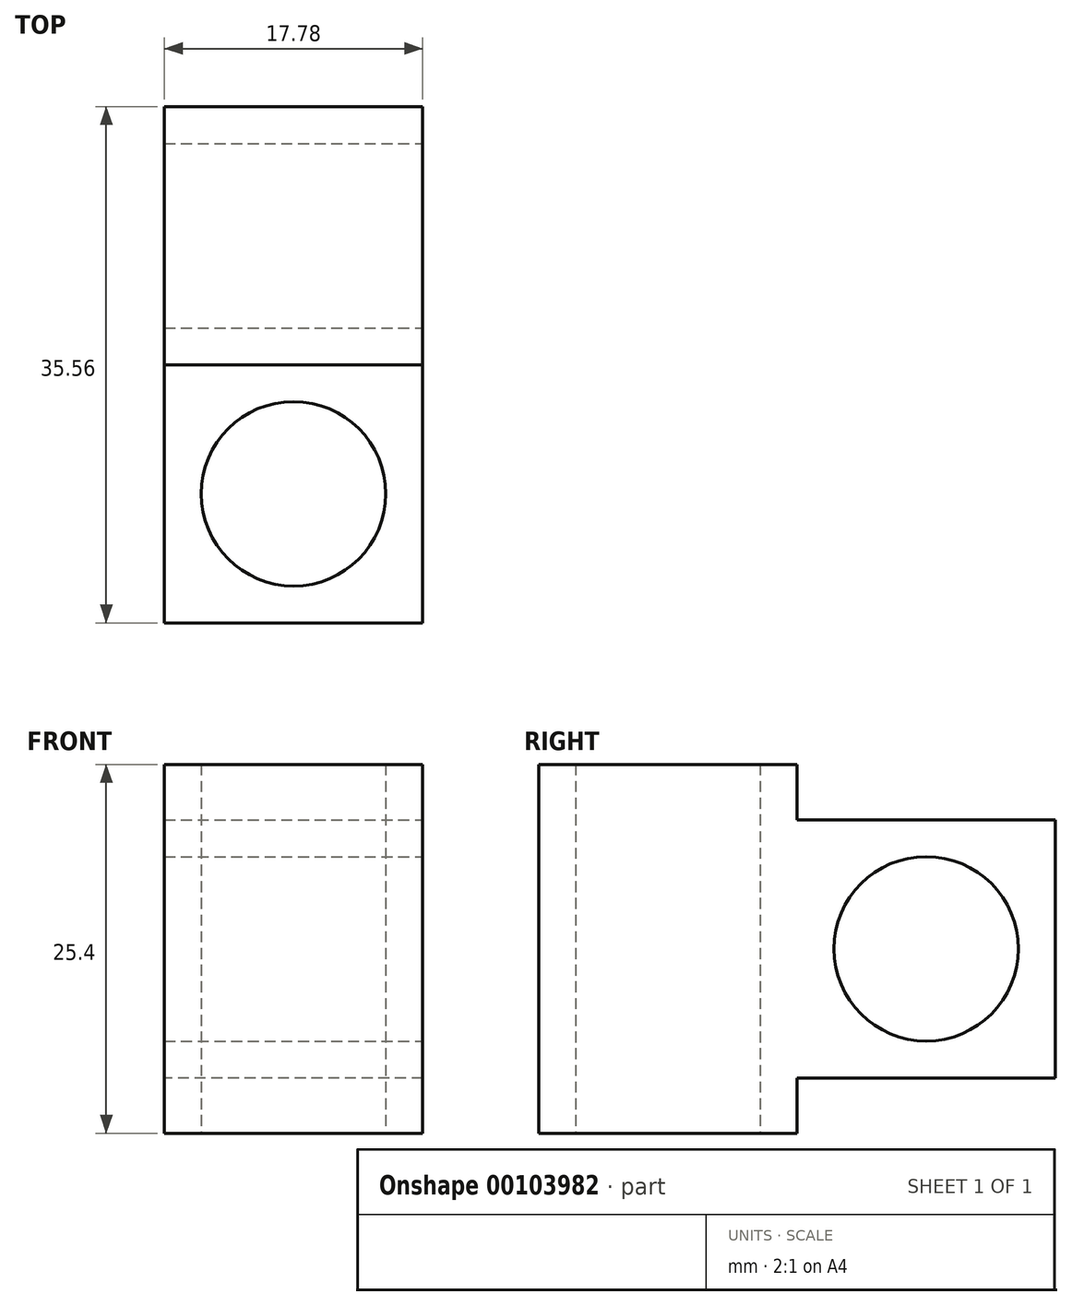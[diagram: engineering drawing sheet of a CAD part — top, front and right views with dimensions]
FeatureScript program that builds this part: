
annotation { "Feature Type Name" : "Feature", "Feature Type Description" : "" }
export const myFeature = defineFeature(function(context is Context, id is Id, definition is map)
    precondition{}
    {
        {
            var Q0;
            Q0=qCreatedBy(makeId("Top.planeOp"),FACE);
            var sketch = newSketch(context, id + "F0", { "sketchPlane" : qUnion([Q0])});
            skCircle(sketch, "E0", {"center": v(-39.15, -30.11) * mm, "radius": 6.35 * mm});
            skLineSegment(sketch, "E1.bottom", {"start": v(-30.26, -21.22) * mm, "end": v(-48.04, -21.22) * mm});
            skLineSegment(sketch, "E1.top", {"start": v(-30.26, -39) * mm, "end": v(-48.04, -39) * mm});
            skLineSegment(sketch, "E1.left", {"start": v(-30.26, -21.22) * mm, "end": v(-30.26, -39) * mm});
            skLineSegment(sketch, "E1.right", {"start": v(-48.04, -21.22) * mm, "end": v(-48.04, -39) * mm});
            skSolve(sketch);
        }
        {
            var Q0;
            Q0=makeQuery(id+"F0.imprint","IMPRINT",FACE,{"disambiguationData":[TD([[makeQuery(id+"F0.imprint","IMPRINT",EDGE,{"derivedFrom":sQuery(id+"F0.wireOp",EDGE,"E0")}),-1.0]])]});
            extrude(context, id + "F1", {"entities" : qUnion([Q0]), "depth" : 25.4 * mm});
        }
        {
            var Q0;
            Q0=makeQuery(id+"F1.opExtrude","SWEPT_FACE",FACE,{"disambiguationData":[OSD([sQuery(id+"F0.wireOp",EDGE,"E1.bottom")])]});
            var sketch = newSketch(context, id + "F2", { "sketchPlane" : qUnion([Q0])});
            skLineSegment(sketch, "E2", {"start": v(30.26, 12.7) * mm, "end": v(48.04, 12.7) * mm, "construction": true});
            skLineSegment(sketch, "E3", {"start": v(39.15, 12.7) * mm, "end": v(48.04, 21.59) * mm, "construction": true});
            skLineSegment(sketch, "E4", {"start": v(48.04, 21.59) * mm, "end": v(30.26, 21.59) * mm});
            skLineSegment(sketch, "E5", {"start": v(30.26, 21.59) * mm, "end": v(30.26, 3.81) * mm});
            skLineSegment(sketch, "E6", {"start": v(30.26, 3.81) * mm, "end": v(48.04, 3.81) * mm});
            skLineSegment(sketch, "E7", {"start": v(48.04, 3.81) * mm, "end": v(48.04, 21.59) * mm});
            skLineSegment(sketch, "E8", {"start": v(39.15, 12.7) * mm, "end": v(30.26, 3.81) * mm, "construction": true});
            skSolve(sketch);
        }
        {
            var Q0;
            Q0 = qSketchRegion(id + "F2", true);
            extrude(context, id + "F3", {"entities" : qUnion([Q0]), "operationType" : NewBodyOperationType.ADD, "depth" : 17.78 * mm});
        }
        {
            var Q0;
            Q0=makeQuery(id+"F3.boolean.opBoolean","MERGE",FACE,{"derivedFrom":[makeQuery(id+"F1.opExtrude","SWEPT_FACE",FACE,{"disambiguationData":[OSD([sQuery(id+"F0.wireOp",EDGE,"E1.left")])]}),makeQuery(id+"F3.opExtrude","SWEPT_FACE",FACE,{"disambiguationData":[OSD([sQuery(id+"F2.wireOp",EDGE,"E5")])]})]});
            var sketch = newSketch(context, id + "F4", { "sketchPlane" : qUnion([Q0])});
            skLineSegment(sketch, "E9", {"start": v(-21.22, 3.81) * mm, "end": v(-3.44, 21.59) * mm, "construction": true});
            skPoint(sketch, "E10", {"position": v(-12.33, 12.7) * mm});
            skSolve(sketch);
        }
        {
            var Q0;
            Q0=sQuery(id+"F4.wireOp",VERTEX,"E10");
            var Q1;
            Q1=makeQuery(id+"F1.opExtrude","SWEPT_BODY",BODY,{"disambiguationData":[OSD([sQuery(id+"F0.wireOp",EDGE,"E0"),sQuery(id+"F0.wireOp",EDGE,"E1.bottom"),sQuery(id+"F0.wireOp",EDGE,"E1.top"),sQuery(id+"F0.wireOp",EDGE,"E1.left"),sQuery(id+"F0.wireOp",EDGE,"E1.right")])]});
            hole(context, id + "F5", {"style" : HoleStyle.SIMPLE, "endStyle" : HoleEndStyle.BLIND, "holeDiameter" : 12.7 * mm, "holeDepth" : 25.4 * mm, "locations" : qUnion([Q0]), "scope" : qUnion([Q1])});
        }
    });
